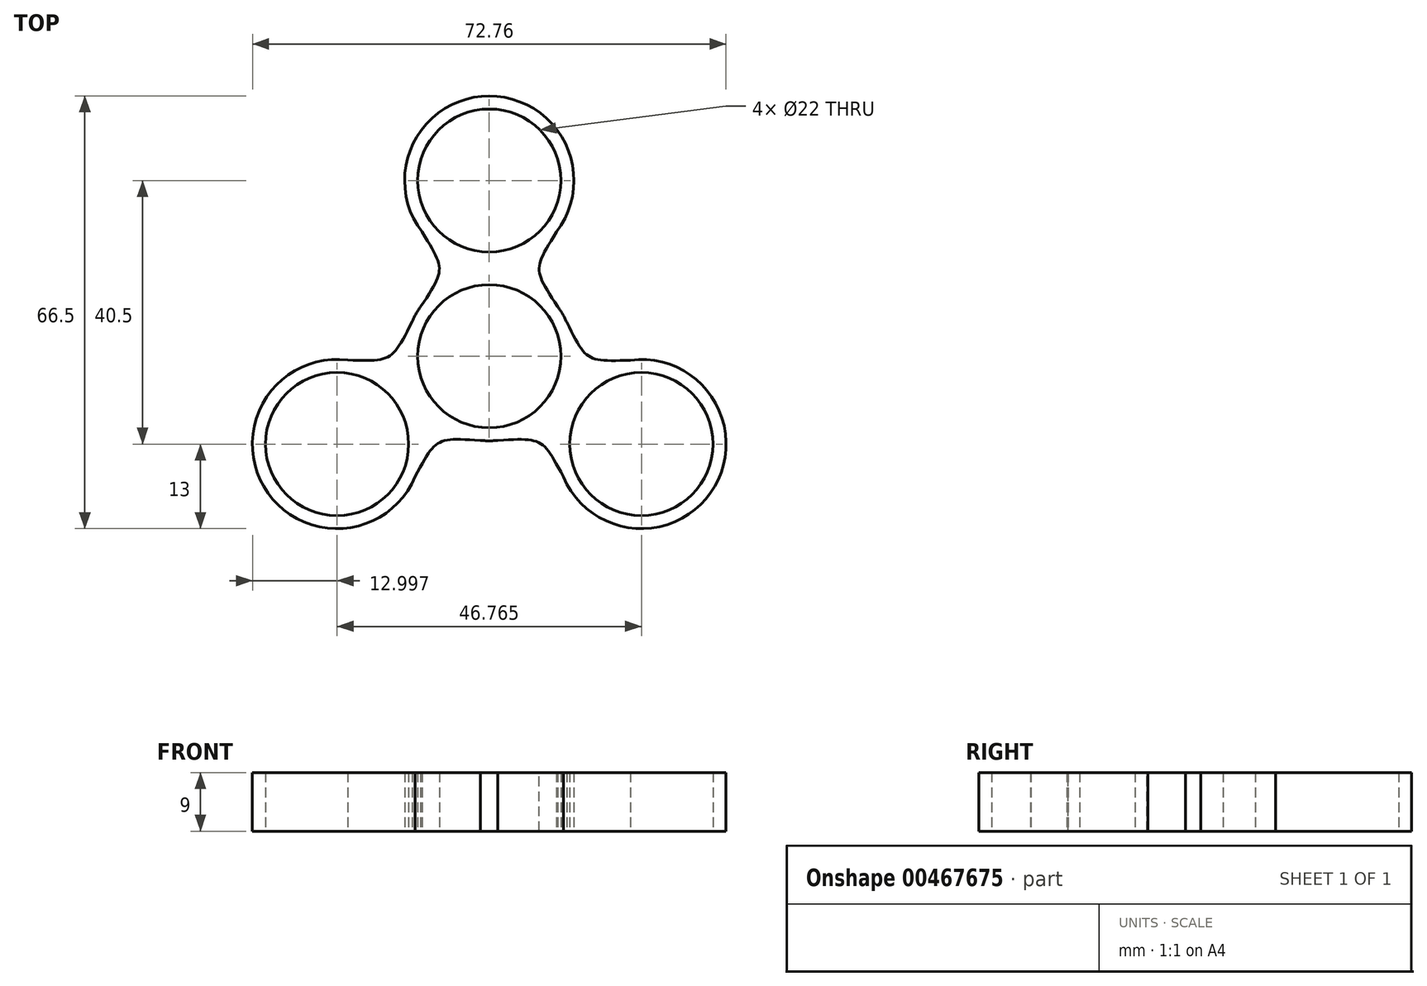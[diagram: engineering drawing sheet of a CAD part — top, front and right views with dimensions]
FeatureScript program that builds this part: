
annotation { "Feature Type Name" : "Feature", "Feature Type Description" : "" }
export const myFeature = defineFeature(function(context is Context, id is Id, definition is map)
    precondition{}
    {
        {
            var Q0;
            Q0=qCreatedBy(makeId("Top.planeOp"),FACE);
            var sketch = newSketch(context, id + "F0", { "sketchPlane" : qUnion([Q0])});
            skCircle(sketch, "E0", {"center": v(0, 0) * mm, "radius": 11 * mm});
            skLineSegment(sketch, "E1", {"start": v(0, 0) * mm, "end": v(0, 27) * mm, "construction": true});
            skCircle(sketch, "E2", {"center": v(0, 27) * mm, "radius": 11 * mm});
            skLineSegment(sketch, "E3", {"start": v(0, 0) * mm, "end": v(-21.08, 36.33) * mm, "construction": true});
            skLineSegment(sketch, "E4", {"start": v(0, 0) * mm, "end": v(20.92, 36.42) * mm, "construction": true});
            skArc(sketch, "E5", {"start": v(-21.08, 36.33) * mm, "mid": v(-0.1, 42) * mm, "end": v(20.92, 36.42) * mm});
            skCircle(sketch, "E6.0", {"center": v(0, 27) * mm, "radius": 13 * mm});
            skCircle(sketch, "E7.0", {"center": v(0, 0) * mm, "radius": 13 * mm});
            skLineSegment(sketch, "E8", {"start": v(-21.08, 36.33) * mm, "end": v(-11.15, 33.69) * mm});
            skLineSegment(sketch, "E9", {"start": v(20.92, 36.42) * mm, "end": v(11.1, 33.77) * mm});
            skPoint(sketch, "E10.1.internal.snap0", {"position": v(-10.54, 18.16) * mm});
            skFitSpline(sketch, "E10", {"points": [v(-10.32, 19.1) * mm, v(-10.54, 7.6) * mm], "startDerivative": vector(10.69, -17.22) * mm, "endDerivative": vector(-11.36, -17.23) * mm});
            skFitSpline(sketch, "E11.MirrorCS", {"points": [v(10.32, 19.1) * mm, v(10.54, 7.6) * mm], "startDerivative": vector(-10.69, -17.22) * mm, "endDerivative": vector(11.36, -17.23) * mm});
            skCircle(sketch, "E12.1.0", {"center": v(-23.38, -13.5) * mm, "radius": 11 * mm});
            skCircle(sketch, "E12.1.1", {"center": v(-23.38, -13.5) * mm, "radius": 13 * mm});
            skArc(sketch, "E12.1.2", {"start": v(-20.92, -36.42) * mm, "mid": v(-36.33, -21.08) * mm, "end": v(-42, -0.1) * mm});
            skLineSegment(sketch, "E12.1.3", {"start": v(-20.92, -36.42) * mm, "end": v(-23.6, -26.5) * mm});
            skLineSegment(sketch, "E12.1.4", {"start": v(-42, -0.1) * mm, "end": v(-34.8, -7.27) * mm});
            skCircle(sketch, "E12.2.0", {"center": v(23.38, -13.5) * mm, "radius": 11 * mm});
            skCircle(sketch, "E12.2.1", {"center": v(23.38, -13.5) * mm, "radius": 13 * mm});
            skArc(sketch, "E12.2.2", {"start": v(42, 0.1) * mm, "mid": v(36.42, -20.92) * mm, "end": v(21.08, -36.33) * mm});
            skLineSegment(sketch, "E12.2.3", {"start": v(42, 0.1) * mm, "end": v(34.75, -7.19) * mm});
            skLineSegment(sketch, "E12.2.4", {"start": v(21.08, -36.33) * mm, "end": v(23.7, -26.5) * mm});
            skFitSpline(sketch, "E13", {"points": [v(21.71, -0.6) * mm, v(11.88, 5.27) * mm], "startDerivative": vector(-20.26, -0.65) * mm, "endDerivative": vector(-9.25, 18.45) * mm});
            skFitSpline(sketch, "E14.MirrorCS", {"points": [v(11.4, -18.54) * mm, v(1.34, -12.93) * mm], "startDerivative": vector(-9.57, 17.87) * mm, "endDerivative": vector(-20.6, -1.22) * mm});
            skFitSpline(sketch, "E15", {"points": [v(-11.38, -18.5) * mm, v(-1.38, -12.93) * mm], "startDerivative": vector(9.57, 17.87) * mm, "endDerivative": vector(20.6, -1.22) * mm});
            skFitSpline(sketch, "E16.MirrorCS", {"points": [v(-21.76, -0.6) * mm, v(-11.87, 5.3) * mm], "startDerivative": vector(20.26, -0.65) * mm, "endDerivative": vector(9.25, 18.45) * mm});
            skSolve(sketch);
        }
        {
            var Q0;
            Q0=makeQuery(id+"F0.imprint","IMPRINT",FACE,{"disambiguationData":[TD([[makeQuery(id+"F0.imprint","IMPRINT",EDGE,{"derivedFrom":sQuery(id+"F0.wireOp",EDGE,"E5")}),-1.0]])]});
            var Q1;
            Q1=makeQuery(id+"F0.imprint","IMPRINT",FACE,{"disambiguationData":[TD([[makeQuery(id+"F0.imprint","IMPRINT",EDGE,{"derivedFrom":sQuery(id+"F0.wireOp",EDGE,"E2")}),-1.0]])]});
            var Q2;
            Q2=makeQuery(id+"F0.imprint","IMPRINT",FACE,{"disambiguationData":[TD([[makeQuery(id+"F0.imprint","IMPRINT",EDGE,{"derivedFrom":sQuery(id+"F0.wireOp",EDGE,"E0")}),-1.0]])]});
            var Q3;
            {var subQ0=sQuery(id+"F0.wireOp",EDGE,"E10");Q3=makeQuery(id+"F0.imprint","IMPRINT",FACE,{"disambiguationData":[TD([[makeQuery(id+"F0.imprint","IMPRINT",EDGE,{"derivedFrom":subQ0}),1.0]])]});}
            var Q4;
            Q4=makeQuery(id+"F0.imprint","IMPRINT",FACE,{"disambiguationData":[TD([[makeQuery(id+"F0.imprint","IMPRINT",EDGE,{"derivedFrom":sQuery(id+"F0.wireOp",EDGE,"E12.1.2")}),-1.0]])]});
            var Q5;
            Q5=makeQuery(id+"F0.imprint","IMPRINT",FACE,{"disambiguationData":[TD([[makeQuery(id+"F0.imprint","IMPRINT",EDGE,{"derivedFrom":sQuery(id+"F0.wireOp",EDGE,"E12.1.0")}),-1.0]])]});
            var Q6;
            {var subQ0=sQuery(id+"F0.wireOp",EDGE,"E15");Q6=makeQuery(id+"F0.imprint","IMPRINT",FACE,{"disambiguationData":[TD([[makeQuery(id+"F0.imprint","IMPRINT",EDGE,{"derivedFrom":subQ0}),1.0]])]});}
            var Q7;
            {var subQ0=sQuery(id+"F0.wireOp",EDGE,"E13");Q7=makeQuery(id+"F0.imprint","IMPRINT",FACE,{"disambiguationData":[TD([[makeQuery(id+"F0.imprint","IMPRINT",EDGE,{"derivedFrom":subQ0}),1.0]])]});}
            var Q8;
            Q8=makeQuery(id+"F0.imprint","IMPRINT",FACE,{"disambiguationData":[TD([[makeQuery(id+"F0.imprint","IMPRINT",EDGE,{"derivedFrom":sQuery(id+"F0.wireOp",EDGE,"E12.2.0")}),-1.0]])]});
            var Q9;
            Q9=makeQuery(id+"F0.imprint","IMPRINT",FACE,{"disambiguationData":[TD([[makeQuery(id+"F0.imprint","IMPRINT",EDGE,{"derivedFrom":sQuery(id+"F0.wireOp",EDGE,"E12.2.2")}),-1.0]])]});
            extrude(context, id + "F1", {"entities" : qUnion([Q0, Q1, Q2, Q3, Q4, Q5, Q6, Q7, Q8, Q9]), "depth" : 9 * mm, "offsetDistance" : 25 * mm});
        }
    });
